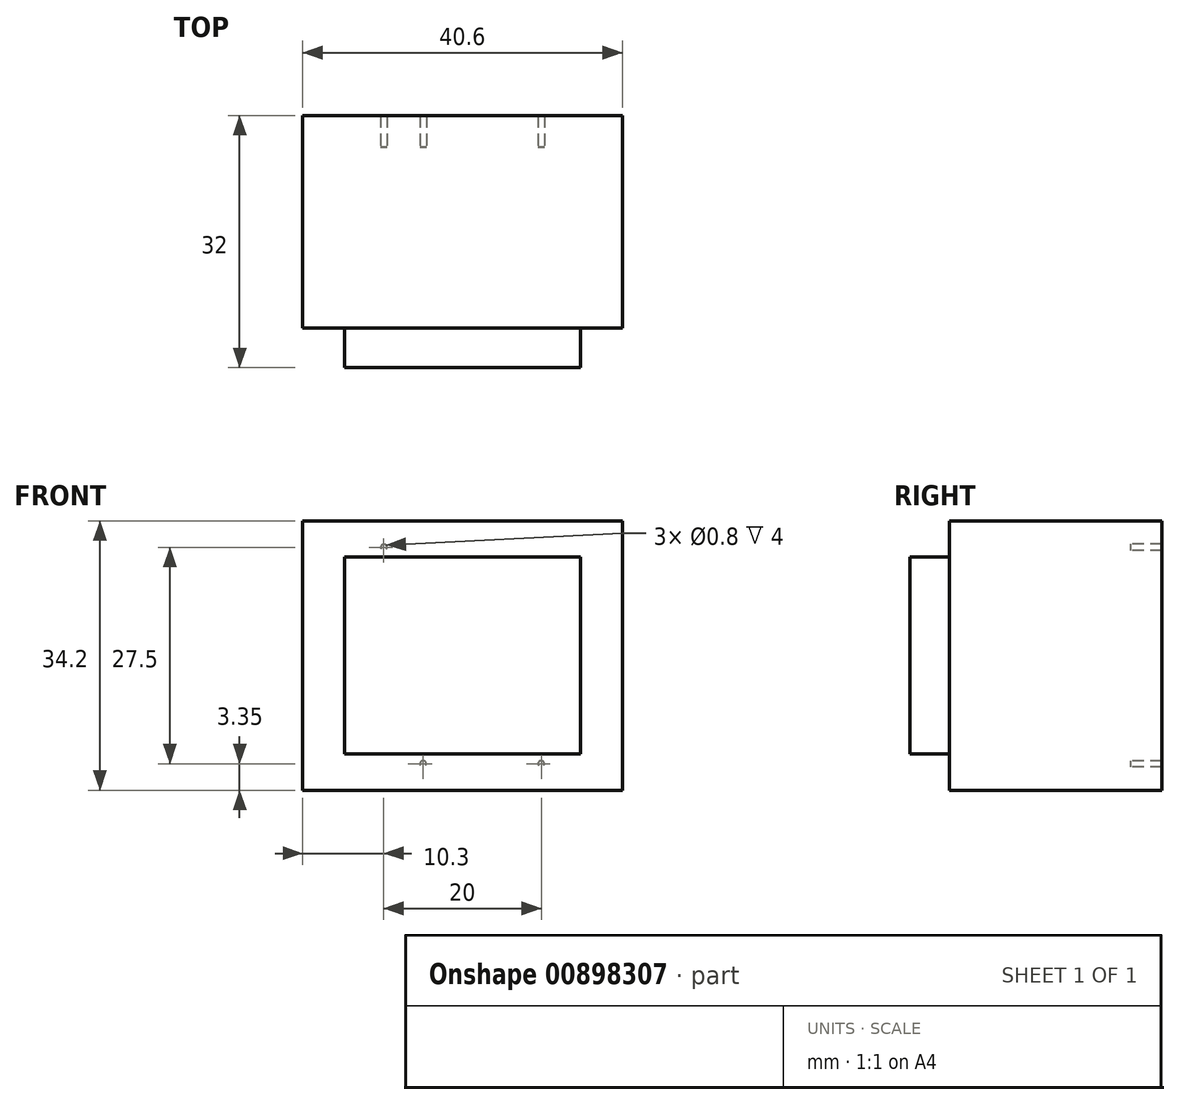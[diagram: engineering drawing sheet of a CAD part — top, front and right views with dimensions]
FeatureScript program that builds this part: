
annotation { "Feature Type Name" : "Feature", "Feature Type Description" : "" }
export const myFeature = defineFeature(function(context is Context, id is Id, definition is map)
    precondition{}
    {
        {
            var Q0;
            Q0=qCreatedBy(makeId("Front.planeOp"),FACE);
            var sketch = newSketch(context, id + "F0", { "sketchPlane" : qUnion([Q0])});
            skLineSegment(sketch, "E0.bottom", {"start": v(-20.3, 17.1) * mm, "end": v(20.3, 17.1) * mm});
            skLineSegment(sketch, "E0.top", {"start": v(-20.3, -17.1) * mm, "end": v(20.3, -17.1) * mm});
            skLineSegment(sketch, "E0.left", {"start": v(-20.3, 17.1) * mm, "end": v(-20.3, -17.1) * mm});
            skLineSegment(sketch, "E0.right", {"start": v(20.3, 17.1) * mm, "end": v(20.3, -17.1) * mm});
            skSolve(sketch);
        }
        {
            var Q0;
            Q0=makeQuery(id+"F0.imprint","IMPRINT",FACE,{"disambiguationData":[TD([[makeQuery(id+"F0.imprint","IMPRINT",EDGE,{"derivedFrom":sQuery(id+"F0.wireOp",EDGE,"E0.bottom")}),-1.0]])]});
            extrude(context, id + "F1", {"entities" : qUnion([Q0]), "depth" : 23 * mm, "offsetDistance" : 25 * mm});
        }
        {
            var Q0;
            Q0=makeQuery(id+"F1.opExtrude","CAP_FACE",FACE,{"disambiguationData":[OSD([sQuery(id+"F0.wireOp",EDGE,"E0.bottom"),sQuery(id+"F0.wireOp",EDGE,"E0.top"),sQuery(id+"F0.wireOp",EDGE,"E0.left"),sQuery(id+"F0.wireOp",EDGE,"E0.right")])],"isStart":false});
            var sketch = newSketch(context, id + "F2", { "sketchPlane" : qUnion([Q0])});
            skLineSegment(sketch, "E1.bottom", {"start": v(-15, 12.5) * mm, "end": v(15, 12.5) * mm});
            skLineSegment(sketch, "E1.top", {"start": v(-15, -12.5) * mm, "end": v(15, -12.5) * mm});
            skLineSegment(sketch, "E1.left", {"start": v(-15, 12.5) * mm, "end": v(-15, -12.5) * mm});
            skLineSegment(sketch, "E1.right", {"start": v(15, 12.5) * mm, "end": v(15, -12.5) * mm});
            skSolve(sketch);
        }
        {
            var Q0;
            Q0=makeQuery(id+"F2.imprint","IMPRINT",FACE,{"disambiguationData":[TD([[makeQuery(id+"F2.imprint","IMPRINT",EDGE,{"derivedFrom":sQuery(id+"F2.wireOp",EDGE,"E1.bottom")}),-1.0]])]});
            extrude(context, id + "F3", {"entities" : qUnion([Q0]), "operationType" : NewBodyOperationType.ADD, "depth" : 5 * mm, "offsetDistance" : 25 * mm});
        }
        {
            var Q0;
            Q0=makeQuery(id+"F1.opExtrude","CAP_FACE",FACE,{"disambiguationData":[OSD([sQuery(id+"F0.wireOp",EDGE,"E0.bottom"),sQuery(id+"F0.wireOp",EDGE,"E0.top"),sQuery(id+"F0.wireOp",EDGE,"E0.left"),sQuery(id+"F0.wireOp",EDGE,"E0.right")])],"isStart":true});
            var sketch = newSketch(context, id + "F4", { "sketchPlane" : qUnion([Q0])});
            skCircle(sketch, "E2", {"center": v(-10, 13.75) * mm, "radius": 0.4 * mm});
            skCircle(sketch, "E3.MirrorC", {"center": v(10, 13.75) * mm, "radius": 0.4 * mm});
            skCircle(sketch, "E4.MirrorC", {"center": v(-10, -13.75) * mm, "radius": 0.4 * mm});
            skCircle(sketch, "E5.MirrorC", {"center": v(10, -13.75) * mm, "radius": 0.4 * mm});
            skCircle(sketch, "E6", {"center": v(-5, -13.75) * mm, "radius": 0.4 * mm});
            skCircle(sketch, "E7.MirrorC", {"center": v(5, -13.75) * mm, "radius": 0.4 * mm});
            skSolve(sketch);
        }
        {
            var Q0;
            Q0=makeQuery(id+"F4.imprint","IMPRINT",FACE,{"disambiguationData":[TD([[makeQuery(id+"F4.imprint","IMPRINT",EDGE,{"derivedFrom":sQuery(id+"F4.wireOp",EDGE,"E3.MirrorC")}),-1.0]])]});
            var Q1;
            Q1=makeQuery(id+"F4.imprint","IMPRINT",FACE,{"disambiguationData":[TD([[makeQuery(id+"F4.imprint","IMPRINT",EDGE,{"derivedFrom":sQuery(id+"F4.wireOp",EDGE,"E2")}),1.0]])]});
            var Q2;
            Q2=makeQuery(id+"F4.imprint","IMPRINT",FACE,{"disambiguationData":[TD([[makeQuery(id+"F4.imprint","IMPRINT",EDGE,{"derivedFrom":sQuery(id+"F4.wireOp",EDGE,"E4.MirrorC")}),-1.0]])]});
            var Q3;
            Q3=makeQuery(id+"F4.imprint","IMPRINT",FACE,{"disambiguationData":[TD([[makeQuery(id+"F4.imprint","IMPRINT",EDGE,{"derivedFrom":sQuery(id+"F4.wireOp",EDGE,"E6")}),1.0]])]});
            var Q4;
            Q4=makeQuery(id+"F4.imprint","IMPRINT",FACE,{"disambiguationData":[TD([[makeQuery(id+"F4.imprint","IMPRINT",EDGE,{"derivedFrom":sQuery(id+"F4.wireOp",EDGE,"E5.MirrorC")}),1.0]])]});
            var Q5;
            Q5=makeQuery(id+"F4.imprint","IMPRINT",FACE,{"disambiguationData":[TD([[makeQuery(id+"F4.imprint","IMPRINT",EDGE,{"derivedFrom":sQuery(id+"F4.wireOp",EDGE,"E7.MirrorC")}),-1.0]])]});
            extrude(context, id + "F5", {"entities" : qUnion([Q0, Q1, Q2, Q3, Q4, Q5]), "operationType" : NewBodyOperationType.ADD, "depth" : 4 * mm, "offsetDistance" : 25 * mm});
        }
    });
